# Revit family: Sanitary_Mirrors_Svedholm_Strato
name_source: partatom
category: Furniture
revit_build: Autodesk Revit 2018 (Build: 20190510_1515(x64)
units: mm (PartAtom-declared; Revit-internal decimal feet)

## family parameters
Cut with Voids When Loaded = No
Host = Face
OmniClass Number = 23.21.11.00
OmniClass Title = Commercial Furniture
Room Calculation Point = No
Shared = No

## types (2) — shared parameters
BIMobject category = Mirrors
Default Elevation = 1219 mm
Description = A mirror with frame in powder coated wire.
Design country = Netherlands
Edition number = 1
IFC Classification = Object
Manufacturer = Svedholm
Manufacturer country = Sweden
Manufacturer name = Svedholm
Masterformat 2014 Code = 08 83 00
Masterformat 2014 Description = Mirrors
Material main = Mirror Glass
Material secondary = Powder coated steel
Model = Strato
NBS Reference Code = 71-55
NBS Reference Description = Mirrors
OmniClass Code = 23-21 37 13 15
OmniClass Description = Mirrors
Product Guid = 86dc34b9-3427-4956-850a-25612a47b870
Product SKU = Strato
Product data url = https://bimobject.com
Product family = Strato
Product group = Mirrors
Product name = Strato
Product url = https://www.svedholm.se
QR code = https://bimobject.com
URL = https://www.svedholm.se
Underconstruction material = Svedholm - Glass - Mirror
Uniclass 1.4 Code = L8732
Uniclass 1.4 Description = Mirrors
Uniclass 2.0 Code = PR-71-55
Uniclass 2.0 Description = Mirrors
Uniclass 2015 Code = Pr_25_71_53
Uniclass 2015 Name = Mirrors

## per-type parameters (varying)
| type | ART - (122.600.001) | ART - (122.600.002) |
| ART - (122.600.002) Dimensions - (700x432mm) | No | Yes |
| ART - (122.600.001) Dimensions - (316x432mm) | Yes | No |

## geometry (parser evidence)
native form markers: Sweep x3
no freeform markers — native parametric forms only
